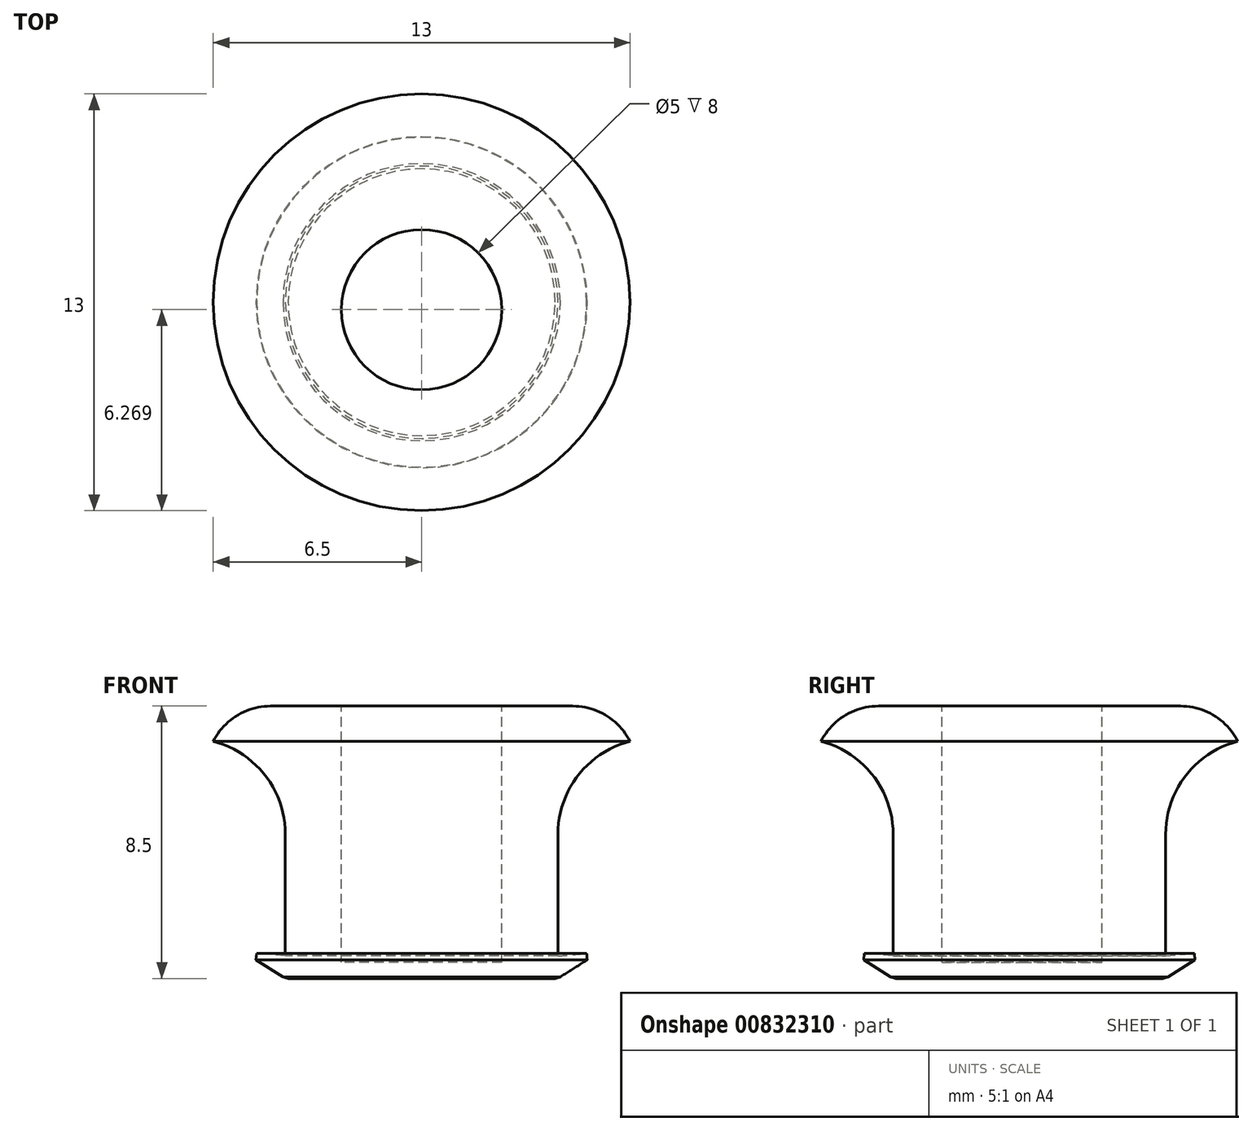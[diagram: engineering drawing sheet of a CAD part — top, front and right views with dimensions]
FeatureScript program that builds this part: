
annotation { "Feature Type Name" : "Feature", "Feature Type Description" : "" }
export const myFeature = defineFeature(function(context is Context, id is Id, definition is map)
    precondition{}
    {
        {
            var Q0;
            Q0=qCreatedBy(makeId("Right.planeOp"),FACE);
            var sketch = newSketch(context, id + "F0", { "sketchPlane" : qUnion([Q0])});
            skLineSegment(sketch, "E0", {"start": v(4.25, -3) * mm, "end": v(4.25, -6.8) * mm});
            skLineSegment(sketch, "E1", {"start": v(4.25, -6.8) * mm, "end": v(5.15, -6.72) * mm});
            skLineSegment(sketch, "E2", {"start": v(4.25, -7.5) * mm, "end": v(4.25, -7.5) * mm});
            skLineSegment(sketch, "E3", {"start": v(4.25, -7.5) * mm, "end": v(0, -7.5) * mm});
            skLineSegment(sketch, "E4", {"start": v(0, 0) * mm, "end": v(0, -7.5) * mm});
            skLineSegment(sketch, "E5", {"start": v(5.15, -6.72) * mm, "end": v(5.16, -6.92) * mm});
            skLineSegment(sketch, "E6", {"start": v(5.16, -6.92) * mm, "end": v(4.25, -7.5) * mm});
            skLineSegment(sketch, "E7", {"start": v(6.5, -0.1) * mm, "end": v(6.5, 1) * mm});
            skLineSegment(sketch, "E8", {"start": v(6.5, 1) * mm, "end": v(0, 1) * mm});
            skLineSegment(sketch, "E9", {"start": v(0, 1) * mm, "end": v(0, 0) * mm});
            skArc(sketch, "E10", {"start": v(6.5, -0.1) * mm, "mid": v(4.88, -1.17) * mm, "end": v(4.25, -3) * mm});
            skSolve(sketch);
        }
        {
            var Q0;
            Q0 = qSketchRegion(id + "F0", true);
            var Q1;
            Q1=sQuery(id+"F0.wireOp",EDGE,"E4");
            revolve(context, id + "F1", {"surfaceOperationType" : NewSurfaceOperationType.NEW, "entities" : qUnion([Q0]), "axis" : qUnion([Q1]), "revolveType" : RevolveType.FULL});
        }
        {
            var Q0;
            Q0=makeQuery(id+"F1.opRevolve","SWEPT_EDGE",EDGE,{"disambiguationData":[OSD([sQuery(id+"F0.wireOp",EDGE,"E2"),sQuery(id+"F0.wireOp",EDGE,"E3")])]});
            chamfer(context, id + "F2", {"entities" : qUnion([Q0]), "width" : .3 * mm, "tangentPropagation" : true});
        }
        {
            var Q0;
            Q0=makeQuery(id+"F1.opRevolve","SWEPT_EDGE",EDGE,{"disambiguationData":[OSD([sQuery(id+"F0.wireOp",EDGE,"E7"),sQuery(id+"F0.wireOp",EDGE,"E8")])]});
            fillet(context, id + "F3", {"entities" : qUnion([Q0]), "radius" : 2 * mm, "tangentPropagation" : true, "allowEdgeOverflow" : false});
        }
        {
            var Q0;
            Q0=makeQuery(id+"F1.opRevolve","SWEPT_FACE",FACE,{"disambiguationData":[OSD([sQuery(id+"F0.wireOp",EDGE,"E8")])]});
            var sketch = newSketch(context, id + "F4", { "sketchPlane" : qUnion([Q0])});
            skCircle(sketch, "E11", {"center": v(0, -0.23) * mm, "radius": 2.5 * mm});
            skSolve(sketch);
        }
        {
            var Q0;
            Q0 = qSketchRegion(id + "F4", true);
            extrude(context, id + "F5", {"entities" : qUnion([Q0]), "operationType" : NewBodyOperationType.REMOVE, "oppositeDirection" : true, "depth" : 8 * mm, "offsetDistance" : 25 * mm});
        }
    });
